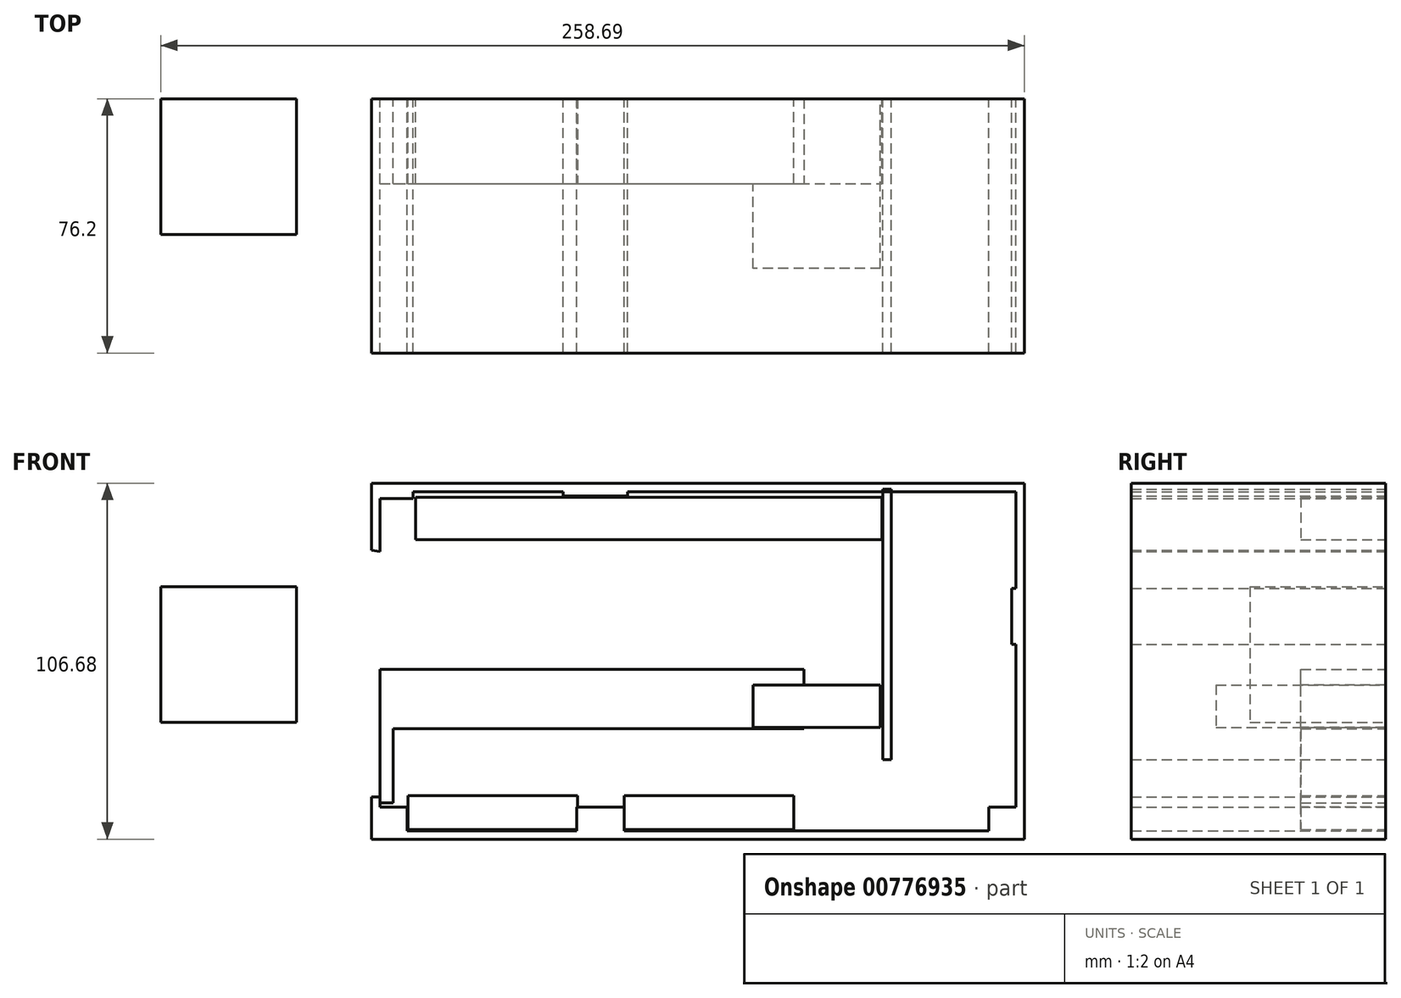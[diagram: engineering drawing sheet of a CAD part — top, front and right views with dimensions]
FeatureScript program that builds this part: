
annotation { "Feature Type Name" : "Feature", "Feature Type Description" : "" }
export const myFeature = defineFeature(function(context is Context, id is Id, definition is map)
    precondition{}
    {
        {
            var Q0;
            Q0=qCreatedBy(makeId("Front.planeOp"),FACE);
            var sketch = newSketch(context, id + "F0", { "sketchPlane" : qUnion([Q0])});
            skLineSegment(sketch, "E0.bottom", {"start": v(-74.65, 57.94) * mm, "end": v(-29.73, 57.94) * mm});
            skLineSegment(sketch, "E0.top", {"start": v(-76.42, -43.66) * mm, "end": v(-25.62, -43.66) * mm});
            skLineSegment(sketch, "E0.left", {"start": v(-84.55, 55.9) * mm, "end": v(-84.55, 39.95) * mm});
            skLineSegment(sketch, "E0.right", {"start": v(105.95, 57.94) * mm, "end": v(105.95, 28.98) * mm});
            skLineSegment(sketch, "E1.0", {"start": v(-87.1, 60.48) * mm, "end": v(108.49, 60.48) * mm});
            skLineSegment(sketch, "E1.1", {"start": v(-87.1, 60.48) * mm, "end": v(-87.1, 40.32) * mm});
            skLineSegment(sketch, "E1.2", {"start": v(-87.1, -46.2) * mm, "end": v(108.49, -46.2) * mm});
            skLineSegment(sketch, "E1.3", {"start": v(108.49, 60.48) * mm, "end": v(108.49, -46.2) * mm});
            skLineSegment(sketch, "E2.top", {"start": v(-84.55, -36.55) * mm, "end": v(-76.42, -36.55) * mm});
            skLineSegment(sketch, "E2.right", {"start": v(-76.42, -43.66) * mm, "end": v(-76.42, -36.55) * mm});
            skLineSegment(sketch, "E3.bottom", {"start": v(-25.62, -36.55) * mm, "end": v(-11.4, -36.55) * mm});
            skLineSegment(sketch, "E3.left", {"start": v(-25.62, -36.55) * mm, "end": v(-25.62, -43.66) * mm});
            skLineSegment(sketch, "E3.right", {"start": v(-11.4, -36.55) * mm, "end": v(-11.4, -43.66) * mm});
            skLineSegment(sketch, "E4.bottom", {"start": v(113.79, -43.66) * mm, "end": v(108.49, -43.66) * mm});
            skPoint(sketch, "E4.top.end.orphan", {"position": v(97.82, -36.55) * mm});
            skLineSegment(sketch, "E5", {"start": v(-84.55, -36.55) * mm, "end": v(-84.55, -33) * mm, "construction": true});
            skLineSegment(sketch, "E6.top", {"start": v(-84.55, -33.5) * mm, "end": v(-87.1, -33.5) * mm});
            skLineSegment(sketch, "E7.trimOffspring", {"start": v(-84.55, -33.5) * mm, "end": v(-84.55, -36.55) * mm});
            skLineSegment(sketch, "E8.trimOffspring", {"start": v(-87.1, -33.5) * mm, "end": v(-87.1, -46.2) * mm});
            skLineSegment(sketch, "E9.top", {"start": v(-84.55, 55.9) * mm, "end": v(-74.65, 55.9) * mm});
            skLineSegment(sketch, "E9.right", {"start": v(-74.65, 57.94) * mm, "end": v(-74.65, 55.9) * mm});
            skLineSegment(sketch, "E10.top", {"start": v(-29.73, 56.67) * mm, "end": v(-10.43, 56.67) * mm});
            skLineSegment(sketch, "E10.left", {"start": v(-29.73, 57.94) * mm, "end": v(-29.73, 56.67) * mm});
            skLineSegment(sketch, "E10.right", {"start": v(-10.43, 57.94) * mm, "end": v(-10.43, 56.67) * mm});
            skLineSegment(sketch, "E11.bottom", {"start": v(105.95, 12.22) * mm, "end": v(104.68, 12.22) * mm});
            skLineSegment(sketch, "E11.top", {"start": v(105.95, 28.98) * mm, "end": v(104.68, 28.98) * mm});
            skLineSegment(sketch, "E11.right", {"start": v(104.68, 12.22) * mm, "end": v(104.68, 28.98) * mm});
            skLineSegment(sketch, "E12.top", {"start": v(105.95, -36.55) * mm, "end": v(97.82, -36.55) * mm});
            skLineSegment(sketch, "E12.right", {"start": v(97.82, -43.66) * mm, "end": v(97.82, -36.55) * mm});
            skLineSegment(sketch, "E13", {"start": v(-87.1, 40.32) * mm, "end": v(-84.55, 39.95) * mm});
            skLineSegment(sketch, "E14", {"start": v(105.67, 57.94) * mm, "end": v(105.67, 29.14) * mm, "construction": true});
            skLineSegment(sketch, "E15.trimOffspring", {"start": v(-10.43, 57.94) * mm, "end": v(105.95, 57.94) * mm});
            skLineSegment(sketch, "E16.trimOffspring", {"start": v(-11.4, -43.66) * mm, "end": v(97.82, -43.66) * mm});
            skLineSegment(sketch, "E17.trimOffspring", {"start": v(105.95, 12.22) * mm, "end": v(105.95, -36.55) * mm});
            skLineSegment(sketch, "E18", {"start": v(119.75, -43.66) * mm, "end": v(119.75, -36.55) * mm, "construction": true});
            skLineSegment(sketch, "E19", {"start": v(105.95, 12.22) * mm, "end": v(105.95, -36.55) * mm, "construction": true});
            skLineSegment(sketch, "E20", {"start": v(-76.42, -43.66) * mm, "end": v(-25.62, -43.66) * mm, "construction": true});
            skLineSegment(sketch, "E21", {"start": v(-11.4, -43.66) * mm, "end": v(97.82, -43.66) * mm, "construction": true});
            skPoint(sketch, "E22.start.orphan", {"position": v(-94.42, -33.5) * mm});
            skLineSegment(sketch, "E23", {"start": v(-84.55, 55.9) * mm, "end": v(-84.55, 39.95) * mm, "construction": true});
            skLineSegment(sketch, "E24", {"start": v(-87.1, -43.66) * mm, "end": v(-87.1, -33.5) * mm, "construction": true});
            skSolve(sketch);
        }
        {
            var Q0;
            Q0=qCreatedBy(makeId("Front.planeOp"),FACE);
            var sketch = newSketch(context, id + "F1", { "sketchPlane" : qUnion([Q0])});
            skLineSegment(sketch, "E25.bottom", {"start": v(-73.88, 56.21) * mm, "end": v(65.82, 56.21) * mm});
            skLineSegment(sketch, "E25.top", {"start": v(-73.88, 43.51) * mm, "end": v(65.82, 43.51) * mm});
            skLineSegment(sketch, "E25.left", {"start": v(-73.88, 56.21) * mm, "end": v(-73.88, 43.51) * mm});
            skLineSegment(sketch, "E25.right", {"start": v(65.82, 56.21) * mm, "end": v(65.82, 43.51) * mm});
            skSolve(sketch);
        }
        {
            var Q0;
            Q0=qCreatedBy(makeId("Front.planeOp"),FACE);
            var sketch = newSketch(context, id + "F2", { "sketchPlane" : qUnion([Q0])});
            skLineSegment(sketch, "E26.bottom", {"start": v(65.35, 0) * mm, "end": v(27.25, 0) * mm});
            skLineSegment(sketch, "E26.top", {"start": v(65.35, -12.7) * mm, "end": v(27.25, -12.7) * mm});
            skLineSegment(sketch, "E26.left", {"start": v(65.35, 0) * mm, "end": v(65.35, -12.7) * mm});
            skLineSegment(sketch, "E26.right", {"start": v(27.25, 0) * mm, "end": v(27.25, -12.7) * mm});
            skSolve(sketch);
        }
        {
            var Q0;
            Q0=makeQuery(id+"F1.imprint","IMPRINT",FACE,{"disambiguationData":[TD([[makeQuery(id+"F1.imprint","IMPRINT",EDGE,{"derivedFrom":sQuery(id+"F1.wireOp",EDGE,"E25.bottom")}),-1.0]])]});
            var sketch = newSketch(context, id + "F3", { "sketchPlane" : qUnion([Q0])});
            skLineSegment(sketch, "E27.bottom", {"start": v(-76.21, -43.36) * mm, "end": v(-25.41, -43.36) * mm});
            skLineSegment(sketch, "E27.top", {"start": v(-76.21, -33.2) * mm, "end": v(-25.41, -33.2) * mm});
            skLineSegment(sketch, "E27.left", {"start": v(-76.21, -43.36) * mm, "end": v(-76.21, -33.2) * mm});
            skLineSegment(sketch, "E27.right", {"start": v(-25.41, -43.36) * mm, "end": v(-25.41, -33.2) * mm});
            skLineSegment(sketch, "E28.bottom", {"start": v(-11.39, -43.36) * mm, "end": v(39.41, -43.36) * mm});
            skLineSegment(sketch, "E28.top", {"start": v(-11.39, -33.2) * mm, "end": v(39.41, -33.2) * mm});
            skLineSegment(sketch, "E28.left", {"start": v(-11.39, -43.36) * mm, "end": v(-11.39, -33.2) * mm});
            skLineSegment(sketch, "E28.right", {"start": v(39.41, -43.36) * mm, "end": v(39.41, -33.2) * mm});
            skPoint(sketch, "E29.start.orphan", {"position": v(-100.16, -43.36) * mm});
            skSolve(sketch);
        }
        {
            var Q0;
            Q0=qCreatedBy(makeId("Front.planeOp"),FACE);
            var sketch = newSketch(context, id + "F4", { "sketchPlane" : qUnion([Q0])});
            skLineSegment(sketch, "E30.bottom", {"start": v(-84.5, -13.12) * mm, "end": v(42.5, -13.12) * mm});
            skLineSegment(sketch, "E30.top", {"start": v(-84.5, 4.66) * mm, "end": v(42.5, 4.66) * mm});
            skLineSegment(sketch, "E30.left", {"start": v(-84.5, -13.12) * mm, "end": v(-84.5, 4.66) * mm});
            skLineSegment(sketch, "E30.right", {"start": v(42.5, -13.12) * mm, "end": v(42.5, 4.66) * mm});
            skLineSegment(sketch, "E31.bottom", {"start": v(-84.5, 4.66) * mm, "end": v(-80.6, 4.66) * mm});
            skLineSegment(sketch, "E31.top", {"start": v(-84.5, -35.34) * mm, "end": v(-80.6, -35.34) * mm});
            skLineSegment(sketch, "E31.left", {"start": v(-84.5, 4.66) * mm, "end": v(-84.5, -35.34) * mm});
            skLineSegment(sketch, "E31.right", {"start": v(-80.6, 4.66) * mm, "end": v(-80.6, -35.34) * mm});
            skSolve(sketch);
        }
        {
            var Q0;
            Q0=qCreatedBy(makeId("Front.planeOp"),FACE);
            var sketch = newSketch(context, id + "F5", { "sketchPlane" : qUnion([Q0])});
            skLineSegment(sketch, "E32.bottom", {"start": v(66.06, 58.62) * mm, "end": v(68.6, 58.62) * mm});
            skLineSegment(sketch, "E32.top", {"start": v(66.06, -22.4) * mm, "end": v(68.6, -22.4) * mm});
            skLineSegment(sketch, "E32.left", {"start": v(66.06, 58.62) * mm, "end": v(66.06, -22.4) * mm});
            skLineSegment(sketch, "E32.right", {"start": v(68.6, 58.62) * mm, "end": v(68.6, -22.4) * mm});
            skSolve(sketch);
        }
        {
            var Q0;
            Q0=qSketchRegion(id+"F0",true);
            var Q1;
            Q1=makeQuery(id+"F5.imprint","IMPRINT",FACE,{"disambiguationData":[TD([[makeQuery(id+"F5.imprint","IMPRINT",EDGE,{"derivedFrom":sQuery(id+"F5.wireOp",EDGE,"E32.bottom")}),-1.0]])]});
            extrude(context, id + "F6", {"entities" : qUnion([Q0, Q1]), "depth" : 76.2 * mm, "offsetDistance" : 25.4 * mm});
        }
        {
            var Q0;
            Q0=makeQuery(id+"F1.imprint","IMPRINT",FACE,{"disambiguationData":[TD([[makeQuery(id+"F1.imprint","IMPRINT",EDGE,{"derivedFrom":sQuery(id+"F1.wireOp",EDGE,"E25.bottom")}),-1.0]])]});
            var Q1;
            Q1=qSketchRegion(id+"F3",true);
            var Q2;
            Q2=makeQuery(id+"F4.imprint","IMPRINT",FACE,{"disambiguationData":[TD([[makeQuery(id+"F4.imprint","IMPRINT",EDGE,{"derivedFrom":sQuery(id+"F4.wireOp",EDGE,"E30.bottom")}),1.0]])]});
            var Q3;
            {var subQ5=sQuery(id+"F4.wireOp",EDGE,"E31.top");Q3=makeQuery(id+"F4.imprint","IMPRINT",FACE,{"disambiguationData":[TD([[makeQuery(id+"F4.imprint","IMPRINT",EDGE,{"derivedFrom":subQ5}),1.0]])]});}
            extrude(context, id + "F7", {"entities" : qUnion([Q0, Q1, Q2, Q3]), "operationType" : NewBodyOperationType.ADD, "depth" : 25.4 * mm, "offsetDistance" : 25.4 * mm});
        }
        {
            var Q0;
            Q0=makeQuery(id+"F2.imprint","IMPRINT",FACE,{"disambiguationData":[TD([[makeQuery(id+"F2.imprint","IMPRINT",EDGE,{"derivedFrom":sQuery(id+"F2.wireOp",EDGE,"E26.bottom")}),1.0]])]});
            extrude(context, id + "F8", {"entities" : qUnion([Q0]), "operationType" : NewBodyOperationType.ADD, "depth" : 50.8 * mm, "offsetDistance" : 25.4 * mm});
        }
        {
            var Q0;
            Q0=qCreatedBy(makeId("Front.planeOp"),FACE);
            var sketch = newSketch(context, id + "F9", { "sketchPlane" : qUnion([Q0])});
            skLineSegment(sketch, "E33.bottom", {"start": v(-150.2, 29.42) * mm, "end": v(-109.56, 29.42) * mm});
            skLineSegment(sketch, "E33.top", {"start": v(-150.2, -11.22) * mm, "end": v(-109.56, -11.22) * mm});
            skLineSegment(sketch, "E33.left", {"start": v(-150.2, 29.42) * mm, "end": v(-150.2, -11.22) * mm});
            skLineSegment(sketch, "E33.right", {"start": v(-109.56, 29.42) * mm, "end": v(-109.56, -11.22) * mm});
            skSolve(sketch);
        }
        {
            var Q0;
            Q0=makeQuery(id+"F9.imprint","IMPRINT",FACE,{"disambiguationData":[TD([[makeQuery(id+"F9.imprint","IMPRINT",EDGE,{"derivedFrom":sQuery(id+"F9.wireOp",EDGE,"E33.bottom")}),-1.0]])]});
            extrude(context, id + "F10", {"entities" : qUnion([Q0]), "depth" : 40.64 * mm, "offsetDistance" : 25.4 * mm});
        }
    });
